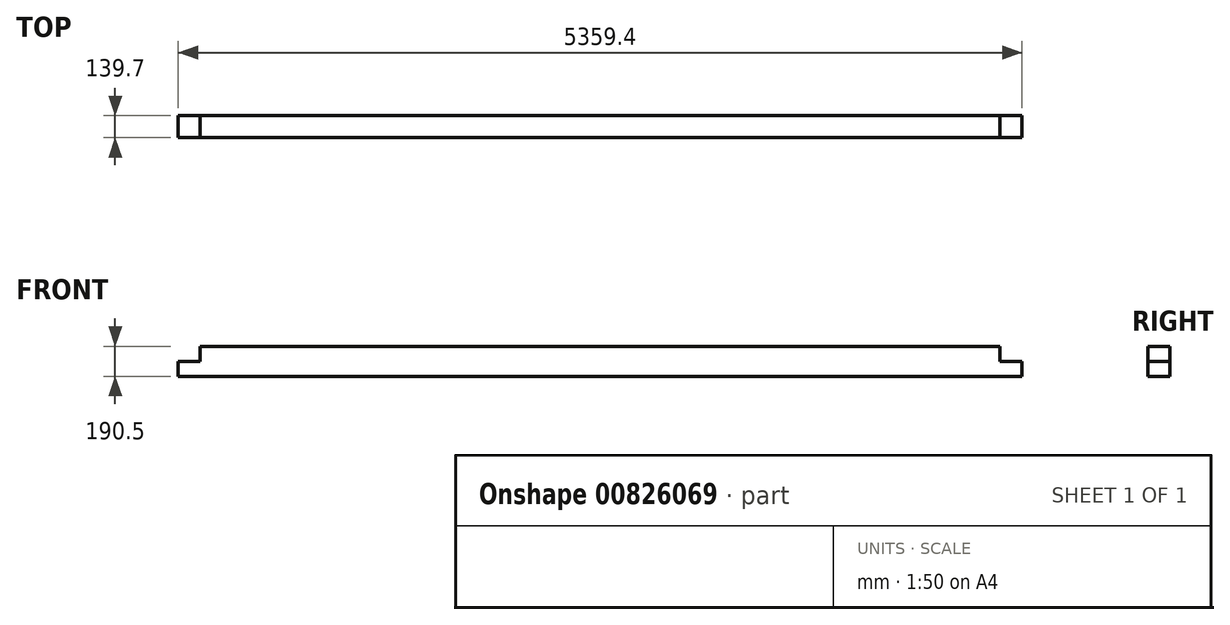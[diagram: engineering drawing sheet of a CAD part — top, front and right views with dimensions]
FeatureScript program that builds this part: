
annotation { "Feature Type Name" : "Feature", "Feature Type Description" : "" }
export const myFeature = defineFeature(function(context is Context, id is Id, definition is map)
    precondition{}
    {
        {
            var Q0;
            Q0=qCreatedBy(makeId("Front.planeOp"),FACE);
            var sketch = newSketch(context, id + "F0", { "sketchPlane" : qUnion([Q0])});
            skLineSegment(sketch, "E0.bottom", {"start": v(181.14, -116.54) * mm, "end": v(2860.84, -116.54) * mm});
            skLineSegment(sketch, "E0.top", {"start": v(181.14, 73.96) * mm, "end": v(5540.54, 73.96) * mm});
            skLineSegment(sketch, "E0.left", {"start": v(181.14, -116.54) * mm, "end": v(181.14, 73.96) * mm});
            skLineSegment(sketch, "E0.right", {"start": v(5540.54, -116.54) * mm, "end": v(5540.54, 73.96) * mm});
            skLineSegment(sketch, "E1.bottom", {"start": v(181.14, 73.96) * mm, "end": v(320.84, 73.96) * mm});
            skLineSegment(sketch, "E1.top", {"start": v(181.14, -21.3) * mm, "end": v(320.84, -21.3) * mm});
            skLineSegment(sketch, "E1.left", {"start": v(181.14, 73.96) * mm, "end": v(181.14, -21.3) * mm});
            skLineSegment(sketch, "E1.right", {"start": v(320.84, 73.96) * mm, "end": v(320.84, -21.3) * mm});
            skLineSegment(sketch, "E2.bottom", {"start": v(2791, -21.3) * mm, "end": v(2930.7, -21.3) * mm});
            skLineSegment(sketch, "E2.top", {"start": v(2791, 73.96) * mm, "end": v(2930.7, 73.96) * mm});
            skLineSegment(sketch, "E2.left", {"start": v(2791, -21.3) * mm, "end": v(2791, 73.96) * mm});
            skLineSegment(sketch, "E2.right", {"start": v(2930.7, -21.3) * mm, "end": v(2930.7, 73.96) * mm});
            skLineSegment(sketch, "E3.bottom", {"start": v(5400.84, -21.3) * mm, "end": v(5540.54, -21.3) * mm});
            skLineSegment(sketch, "E3.top", {"start": v(5400.84, 73.96) * mm, "end": v(5540.54, 73.96) * mm});
            skLineSegment(sketch, "E3.left", {"start": v(5400.84, -21.3) * mm, "end": v(5400.84, 73.96) * mm});
            skLineSegment(sketch, "E3.right", {"start": v(5540.54, -21.3) * mm, "end": v(5540.54, 73.96) * mm});
            skLineSegment(sketch, "E4", {"start": v(2860.84, -116.54) * mm, "end": v(5540.54, -116.54) * mm});
            skSolve(sketch);
        }
        {
            var Q0;
            Q0=makeQuery(id+"F0.imprint","IMPRINT",FACE,{"disambiguationData":[TD([[makeQuery(id+"F0.imprint","IMPRINT",EDGE,{"derivedFrom":sQuery(id+"F0.wireOp",EDGE,"E0.bottom")}),1.0]])]});
            var Q1;
            Q1=makeQuery(id+"F0.imprint","IMPRINT",FACE,{"disambiguationData":[TD([[makeQuery(id+"F0.imprint","IMPRINT",EDGE,{"derivedFrom":sQuery(id+"F0.wireOp",EDGE,"E2.bottom")}),1.0]])]});
            extrude(context, id + "F1", {"entities" : qUnion([Q0, Q1]), "depth" : 139.7 * mm, "offsetDistance" : 25.4 * mm});
        }
    });
